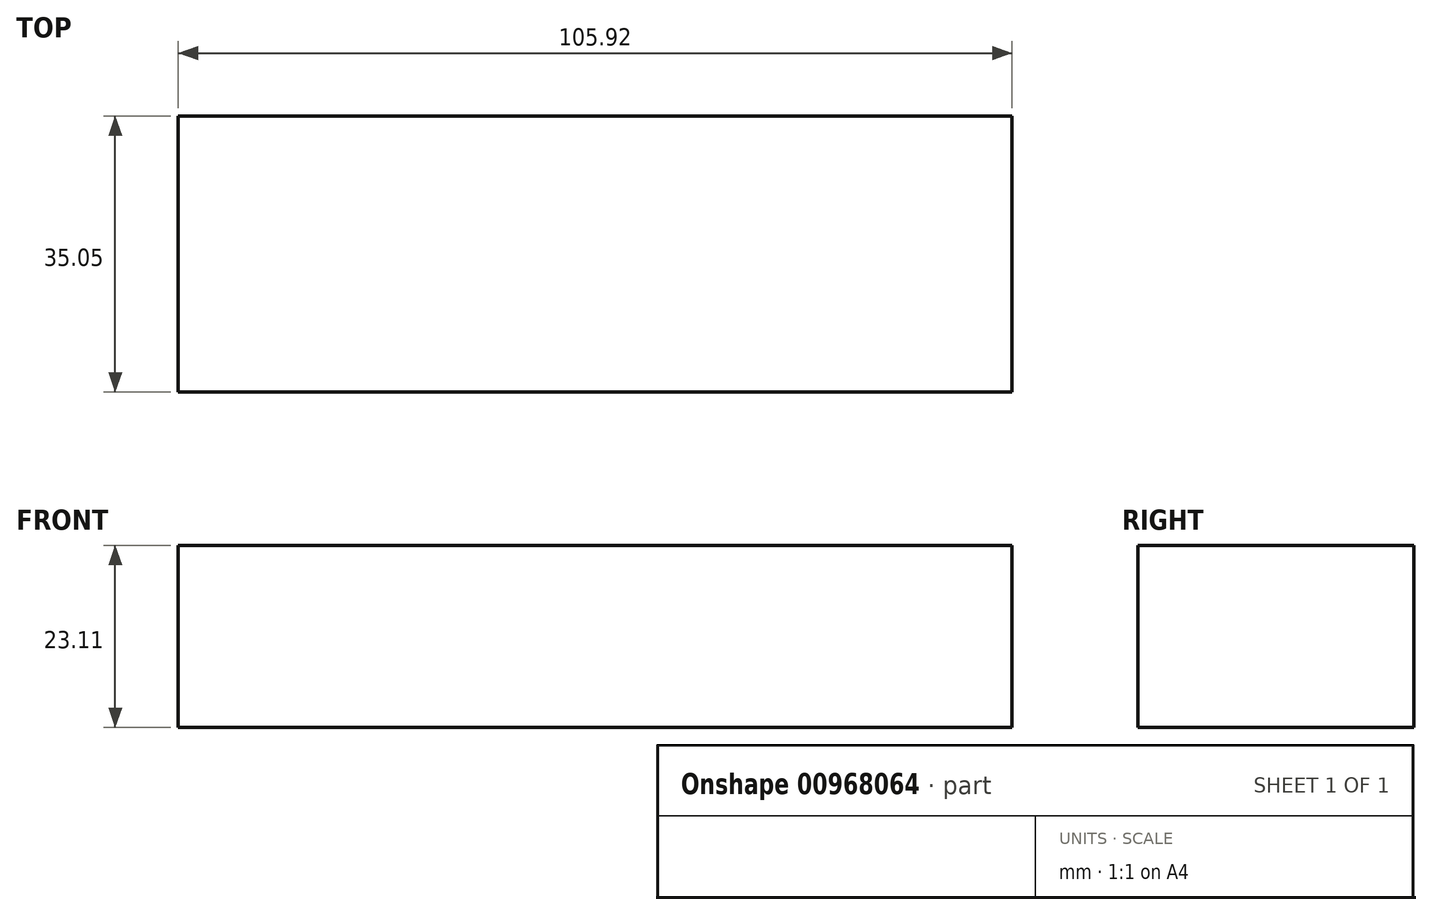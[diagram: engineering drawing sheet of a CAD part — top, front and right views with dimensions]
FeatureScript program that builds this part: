
annotation { "Feature Type Name" : "Feature", "Feature Type Description" : "" }
export const myFeature = defineFeature(function(context is Context, id is Id, definition is map)
    precondition{}
    {
        {
            var Q0;
            Q0=qCreatedBy(makeId("Top.planeOp"),FACE);
            var sketch = newSketch(context, id + "F0", { "sketchPlane" : qUnion([Q0])});
            skLineSegment(sketch, "E0.bottom", {"start": v(0, 0) * mm, "end": v(105.92, 0) * mm});
            skLineSegment(sketch, "E0.top", {"start": v(0, 35.05) * mm, "end": v(105.92, 35.05) * mm});
            skLineSegment(sketch, "E0.left", {"start": v(0, 0) * mm, "end": v(0, 35.05) * mm});
            skLineSegment(sketch, "E0.right", {"start": v(105.92, 0) * mm, "end": v(105.92, 35.05) * mm});
            skSolve(sketch);
        }
        {
            var Q0;
            Q0=makeQuery(id+"F0.imprint","IMPRINT",FACE,{"disambiguationData":[TD([[makeQuery(id+"F0.imprint","IMPRINT",EDGE,{"derivedFrom":sQuery(id+"F0.wireOp",EDGE,"E0.bottom")}),1.0]])]});
            extrude(context, id + "F1", {"entities" : qUnion([Q0]), "depth" : 23.1 * mm, "offsetDistance" : 25 * mm});
        }
    });
